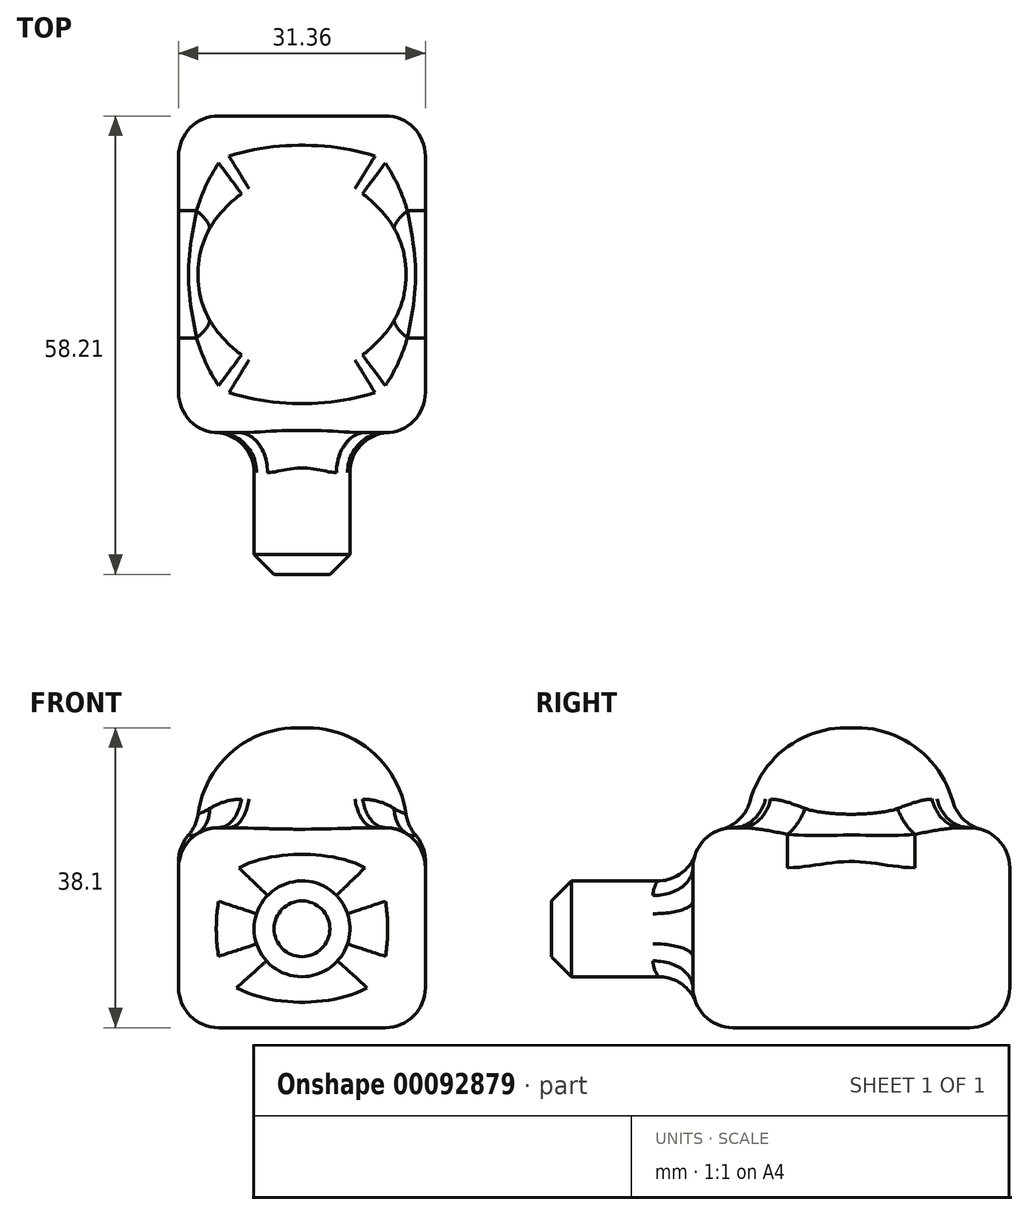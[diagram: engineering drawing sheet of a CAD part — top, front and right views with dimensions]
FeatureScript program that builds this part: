
annotation { "Feature Type Name" : "Feature", "Feature Type Description" : "" }
export const myFeature = defineFeature(function(context is Context, id is Id, definition is map)
    precondition{}
    {
        {
            var Q0;
            Q0=qCreatedBy(makeId("Top.planeOp"),FACE);
            var sketch = newSketch(context, id + "F0", { "sketchPlane" : qUnion([Q0])});
            skLineSegment(sketch, "E0.bottom", {"start": v(15.68, 20.11) * mm, "end": v(-15.68, 20.11) * mm});
            skLineSegment(sketch, "E0.top", {"start": v(15.68, -20.11) * mm, "end": v(-15.68, -20.11) * mm});
            skLineSegment(sketch, "E0.left", {"start": v(15.68, 20.11) * mm, "end": v(15.68, -20.11) * mm});
            skLineSegment(sketch, "E0.right", {"start": v(-15.68, 20.11) * mm, "end": v(-15.68, -20.11) * mm});
            skPoint(sketch, "E0.middle", {"position": v(0, 0) * mm});
            skCircle(sketch, "E1", {"center": v(0, 0) * mm, "radius": 13.33 * mm});
            skSolve(sketch);
        }
        {
            var Q0;
            Q0=makeQuery(id+"F0.imprint","IMPRINT",FACE,{"disambiguationData":[TD([[makeQuery(id+"F0.imprint","IMPRINT",EDGE,{"derivedFrom":sQuery(id+"F0.wireOp",EDGE,"E0.bottom")}),1.0]])]});
            extrude(context, id + "F1", {"entities" : qUnion([Q0]), "depth" : 25.4 * mm});
        }
        {
            var Q0;
            Q0=makeQuery(id+"F0.imprint","IMPRINT",FACE,{"disambiguationData":[TD([[makeQuery(id+"F0.imprint","IMPRINT",EDGE,{"derivedFrom":sQuery(id+"F0.wireOp",EDGE,"E1")}),1.0]])]});
            extrude(context, id + "F2", {"entities" : qUnion([Q0]), "operationType" : NewBodyOperationType.ADD, "depth" : 38.1 * mm});
        }
        {
            var Q0;
            Q0=makeQuery(id+"F2.opExtrude","CAP_EDGE",EDGE,{"disambiguationData":[OSD([sQuery(id+"F0.wireOp",EDGE,"E1")])],"isStart":false});
            fillet(context, id + "F3", {"entities" : qUnion([Q0]), "radius" : 12.7 * mm, "tangentPropagation" : true, "allowEdgeOverflow" : false});
        }
        {
            var Q0;
            Q0=makeQuery(id+"F1.opExtrude","CAP_EDGE",EDGE,{"disambiguationData":[OSD([sQuery(id+"F0.wireOp",EDGE,"E0.left")])],"isStart":false});
            var Q1;
            Q1=makeQuery(id+"F1.opExtrude","CAP_EDGE",EDGE,{"disambiguationData":[OSD([sQuery(id+"F0.wireOp",EDGE,"E0.left")])],"isStart":true});
            var Q2;
            Q2=makeQuery(id+"F1.opExtrude","SWEPT_EDGE",EDGE,{"disambiguationData":[OSD([sQuery(id+"F0.wireOp",EDGE,"E0.top"),sQuery(id+"F0.wireOp",EDGE,"E0.left")])]});
            var Q3;
            Q3=makeQuery(id+"F1.opExtrude","SWEPT_EDGE",EDGE,{"disambiguationData":[OSD([sQuery(id+"F0.wireOp",EDGE,"E0.top"),sQuery(id+"F0.wireOp",EDGE,"E0.right")])]});
            var Q4;
            Q4=makeQuery(id+"F1.opExtrude","CAP_EDGE",EDGE,{"disambiguationData":[OSD([sQuery(id+"F0.wireOp",EDGE,"E0.right")])],"isStart":false});
            var Q5;
            Q5=makeQuery(id+"F1.opExtrude","CAP_EDGE",EDGE,{"disambiguationData":[OSD([sQuery(id+"F0.wireOp",EDGE,"E0.right")])],"isStart":true});
            var Q6;
            Q6=makeQuery(id+"F1.opExtrude","CAP_EDGE",EDGE,{"disambiguationData":[OSD([sQuery(id+"F0.wireOp",EDGE,"E0.top")])],"isStart":false});
            var Q7;
            Q7=makeQuery(id+"F1.opExtrude","CAP_EDGE",EDGE,{"disambiguationData":[OSD([sQuery(id+"F0.wireOp",EDGE,"E0.top")])],"isStart":true});
            var Q8;
            Q8=makeQuery(id+"F1.opExtrude","CAP_EDGE",EDGE,{"disambiguationData":[OSD([sQuery(id+"F0.wireOp",EDGE,"E0.bottom")])],"isStart":false});
            var Q9;
            Q9=makeQuery(id+"F1.opExtrude","SWEPT_EDGE",EDGE,{"disambiguationData":[OSD([sQuery(id+"F0.wireOp",EDGE,"E0.bottom"),sQuery(id+"F0.wireOp",EDGE,"E0.right")])]});
            var Q10;
            Q10=makeQuery(id+"F1.opExtrude","CAP_EDGE",EDGE,{"disambiguationData":[OSD([sQuery(id+"F0.wireOp",EDGE,"E0.bottom")])],"isStart":true});
            var Q11;
            Q11=makeQuery(id+"F1.opExtrude","SWEPT_EDGE",EDGE,{"disambiguationData":[OSD([sQuery(id+"F0.wireOp",EDGE,"E0.bottom"),sQuery(id+"F0.wireOp",EDGE,"E0.left")])]});
            fillet(context, id + "F4", {"entities" : qUnion([Q0, Q1, Q2, Q3, Q4, Q5, Q6, Q7, Q8, Q9, Q10, Q11]), "radius" : 5.08 * mm, "tangentPropagation" : true, "allowEdgeOverflow" : false});
        }
        {
            var Q0;
            Q0=makeQuery(id+"F4.opFillet","BLEND_EDGE",EDGE,{"blendedFrom":[makeQuery(id+"F1.opExtrude","CAP_EDGE",EDGE,{"disambiguationData":[OSD([sQuery(id+"F0.wireOp",EDGE,"E0.left")])],"isStart":false}),makeQuery(id+"F3.opFillet","BLEND_FACE",FACE,{"disambiguationData":[OSD([sQuery(id+"F0.wireOp",EDGE,"E1")])]})],"blendedInto":[makeQuery(id+"F3.opFillet","BLEND_FACE",FACE,{"disambiguationData":[OSD([sQuery(id+"F0.wireOp",EDGE,"E1")])]})]});
            fillet(context, id + "F5", {"entities" : qUnion([Q0]), "radius" : 5.08 * mm, "tangentPropagation" : true, "allowEdgeOverflow" : false});
        }
        {
            var Q0;
            Q0=qCreatedBy(makeId("Front.planeOp"),FACE);
            var sketch = newSketch(context, id + "F6", { "sketchPlane" : qUnion([Q0])});
            skCircle(sketch, "E2", {"center": v(0, 12.56) * mm, "radius": 6.08 * mm});
            skSolve(sketch);
        }
        {
            var Q0;
            Q0=makeQuery(id+"F6.imprint","IMPRINT",FACE,{"disambiguationData":[TD([[makeQuery(id+"F6.imprint","IMPRINT",EDGE,{"derivedFrom":sQuery(id+"F6.wireOp",EDGE,"E2")}),1.0]])]});
            extrude(context, id + "F7", {"entities" : qUnion([Q0]), "operationType" : NewBodyOperationType.ADD, "depth" : 38.1 * mm});
        }
        {
            var Q0;
            Q0=makeQuery(id+"F7.opExtrude","CAP_EDGE",EDGE,{"disambiguationData":[OSD([sQuery(id+"F6.wireOp",EDGE,"E2")])],"isStart":false});
            chamfer(context, id + "F8", {"entities" : qUnion([Q0]), "width" : 2.54 * mm, "tangentPropagation" : true});
        }
        {
            var Q0;
            Q0=makeQuery(id+"F7.boolean.opBoolean","INTERSECT",EDGE,{"derivedFrom":[makeQuery(id+"F1.opExtrude","SWEPT_FACE",FACE,{"disambiguationData":[OSD([sQuery(id+"F0.wireOp",EDGE,"E0.top")])]}),makeQuery(id+"F7.opExtrude","SWEPT_FACE",FACE,{"disambiguationData":[OSD([sQuery(id+"F6.wireOp",EDGE,"E2")])]})]});
            fillet(context, id + "F9", {"entities" : qUnion([Q0]), "radius" : 5.08 * mm, "tangentPropagation" : true, "allowEdgeOverflow" : false});
        }
    });
